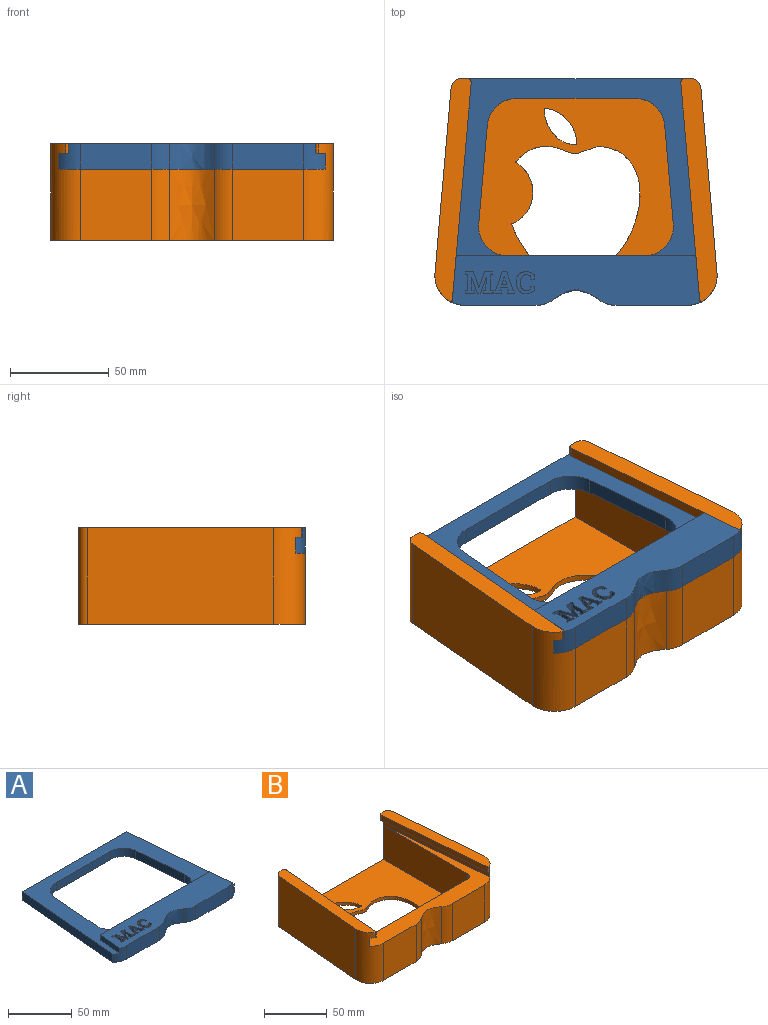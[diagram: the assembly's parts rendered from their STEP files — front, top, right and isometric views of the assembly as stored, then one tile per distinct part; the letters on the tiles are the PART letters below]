
ASSEMBLY  parts=2 mates=1
PART A: 101 faces, bbox 135.2x115x13 mm
  f0: plane 125.76x25mm, normal (0,0,1), area 2737.2mm2, adj f3,f4,f5,f6,f7,f11,f12,f15
  f1: plane 135.17x113.64mm, normal (0,0,1), area 3992.9mm2, adj f7,f8,f9,f10,f11,f13,f14,f15
  f2: plane 135.17x115mm, normal (0,0,-1), area 6927.4mm2, adj f3,f4,f5,f6,f7,f8,f9,f10
  f3: cylinder r=15mm len=13mm, axis (0,0,-1), area 125.4mm2, adj f0,f2,f4,f12
  f4: extruded ~22.62x13mm, area 325.1mm2, adj f0,f2,f3,f5
  f5: cylinder r=15mm len=13mm, axis (0,0,-1), area 125.4mm2, adj f0,f2,f4,f6
  f6: plane 36.33x13mm, normal (0,-1,0), area 472.3mm2, adj f0,f2,f5,f7
  f7: cylinder r=15mm len=13mm, axis (0,0,-1), area 130.4mm2, adj f0,f1,f2,f6,f8,f22
  f8: plane 110.25x9.59mm, normal (1,0.09,0), area 885.4mm2, adj f1,f2,f7,f9
  f9: plane 116x8mm, normal (0,1,0), area 928mm2, adj f1,f2,f8,f10
  f10: plane 110.25x9.59mm, normal (-1,0.09,0), area 885.4mm2, adj f1,f2,f9,f11
  f11: cylinder r=15mm len=13mm, axis (0,0,-1), area 130.4mm2, adj f0,f1,f2,f10,f12,f21
  f12: plane 36.33x13mm, normal (0,-1,0), area 472.3mm2, adj f0,f2,f3,f11
  f13: plane 60.16x8mm, normal (0,-1,0), area 481.3mm2, adj f1,f2,f17,f20
  f14: plane 50x8mm, normal (1,-0.09,0), area 401.5mm2, adj f1,f2,f17,f18
  f15: plane 121.65x13mm, normal (0,1,0), area 1159.1mm2, adj f0,f1,f2,f18,f19,f21,f22
  f16: plane 50x8mm, normal (-1,-0.09,0), area 401.5mm2, adj f1,f2,f19,f20
  f17: cylinder r=15mm len=14.94mm, axis (0,0,-1), area 178.1mm2, adj f1,f2,f13,f14
  f18: cylinder r=15mm len=16.3mm, axis (0,0,-1), area 198.9mm2, adj f1,f2,f14,f15
  f19: cylinder r=15mm len=16.3mm, axis (0,0,-1), area 198.9mm2, adj f1,f2,f15,f16
  f20: cylinder r=15mm len=14.94mm, axis (0,0,-1), area 178.1mm2, adj f1,f2,f13,f16
  f21: plane 23.64x5mm, normal (-1,0.09,0), area 118.6mm2, adj f0,f1,f11,f15
  f22: plane 23.64x5mm, normal (1,0.09,0), area 118.6mm2, adj f0,f1,f7,f15
  f23: plane 5x2.54mm, normal (0,-1,0), area 12.7mm2, adj f24,f42,f43,f100
  f24: plane 5x3.9mm, normal (-0.95,0.3,0), area 20.5mm2, adj f23,f25,f43,f100
  f25: plane 5x0.04mm, normal (0,1,0), area 0.2mm2, adj f24,f42,f43,f100
  f26: plane 5x0.79mm, normal (0.14,-0.99,0), area 4mm2, adj f0,f27,f41,f43
  f27: plane 5x1.33mm, normal (1,0,0), area 6.7mm2, adj f0,f26,f28,f43
  f28: plane 5x3.77mm, normal (0,1,0), area 18.9mm2, adj f0,f27,f29,f43
  f29: plane 5x1.33mm, normal (-1,0,0), area 6.7mm2, adj f0,f28,f30,f43
  f30: plane 5x0.77mm, normal (-0.18,-0.98,0), area 3.9mm2, adj f0,f29,f31,f43
  f31: plane 5x1.52mm, normal (-0.95,0.3,0), area 8mm2, adj f0,f30,f32,f43
  f32: plane 5x3.59mm, normal (0,1,0), area 18mm2, adj f0,f31,f33,f43
  f33: plane 5x1.52mm, normal (0.95,0.3,0), area 8mm2, adj f0,f32,f34,f43
  f34: plane 5x0.77mm, normal (0.17,-0.98,0), area 3.9mm2, adj f0,f33,f35,f43
  f35: plane 5x1.33mm, normal (1,0,0), area 6.7mm2, adj f0,f34,f36,f43
  f36: plane 5x3.77mm, normal (0,1,0), area 18.9mm2, adj f0,f35,f37,f43
  f37: plane 5x1.33mm, normal (-1,0,0), area 6.7mm2, adj f0,f36,f38,f43
  f38: plane 5x0.79mm, normal (-0.14,-0.99,0), area 4mm2, adj f0,f37,f39,f43
  f39: plane 9.63x5mm, normal (-0.94,-0.33,0), area 51mm2, adj f0,f38,f40,f43
  f40: plane 5x2.27mm, normal (0,-1,0), area 11.4mm2, adj f0,f39,f41,f43
  f41: plane 9.63x5mm, normal (0.94,-0.33,0), area 51mm2, adj f0,f26,f40,f43
  f42: plane 5x3.9mm, normal (0.95,0.3,0), area 20.5mm2, adj f23,f25,f43,f100
  f43: plane 11.08x10.58mm, normal (0,0,1), area 53.7mm2, adj f23,f24,f25,f26,f27,f28,f29,f30
  f44: plane 5x1.65mm, normal (0,1,0), area 8.3mm2, adj f0,f45,f67,f68
  f45: plane 5x2.19mm, normal (-1,0,0), area 11mm2, adj f0,f44,f46,f68
  f46: extruded ~5x1.71mm, area 10.6mm2, adj f0,f45,f47,f68
  f47: extruded ~5x2.32mm, area 11.9mm2, adj f0,f46,f48,f68
  f48: extruded ~5x3.66mm, area 20.5mm2, adj f0,f47,f49,f68
  f49: extruded ~5x3.97mm, area 21.6mm2, adj f0,f48,f50,f68
  f50: plane 5x0.37mm, normal (1,0,0), area 1.9mm2, adj f0,f49,f51,f68
  f51: extruded ~5x3.97mm, area 21.6mm2, adj f0,f50,f52,f68
  f52: extruded ~5x3.65mm, area 20.4mm2, adj f0,f51,f53,f68
  f53: extruded ~5x2.32mm, area 11.9mm2, adj f0,f52,f54,f68
  f54: extruded ~5x1.71mm, area 10.6mm2, adj f0,f53,f55,f68
  f55: plane 5x2.19mm, normal (-1,0,0), area 11mm2, adj f0,f54,f56,f68
  f56: plane 5x1.65mm, normal (0,-1,0), area 8.3mm2, adj f0,f55,f57,f68
  f57: plane 5x1.48mm, normal (0.99,-0.15,0), area 7.5mm2, adj f0,f56,f58,f68
  f58: extruded ~5x0.84mm, area 5mm2, adj f0,f57,f59,f68
  f59: extruded ~5x1.2mm, area 6.1mm2, adj f0,f58,f60,f68
  f60: extruded ~5x2.19mm, area 12.7mm2, adj f0,f59,f61,f68
  f61: extruded ~5x2.75mm, area 14.5mm2, adj f0,f60,f62,f68
  f62: plane 5x0.39mm, normal (-1,0,0), area 1.9mm2, adj f0,f61,f63,f68
  f63: extruded ~5x2.74mm, area 14.5mm2, adj f0,f62,f64,f68
  f64: extruded ~5x2.22mm, area 12.8mm2, adj f0,f63,f65,f68
  f65: extruded ~5x1.18mm, area 6mm2, adj f0,f64,f66,f68
  f66: extruded ~5x0.82mm, area 4.9mm2, adj f0,f65,f67,f68
  f67: plane 5x1.48mm, normal (0.99,0.15,0), area 7.5mm2, adj f0,f44,f66,f68
  f68: plane 11.4x9.11mm, normal (0,0,1), area 46.6mm2, adj f44,f45,f46,f47,f48,f49,f50,f51
  f69: plane 5x0.05mm, normal (0.16,0.99,0), area 0.2mm2, adj f0,f70,f98,f99
  f70: plane 5x4.9mm, normal (1,-0.04,0), area 24.5mm2, adj f0,f69,f71,f99
  f71: plane 5x1.74mm, normal (1,0,0), area 8.7mm2, adj f0,f70,f72,f99
  f72: plane 5x1.18mm, normal (0.19,-0.98,0), area 6mm2, adj f0,f71,f73,f99
  f73: plane 5x1.33mm, normal (1,0,0), area 6.7mm2, adj f0,f72,f74,f99
  f74: plane 5x4.59mm, normal (0,1,0), area 22.9mm2, adj f0,f73,f75,f99
  f75: plane 5x1.33mm, normal (-1,0,0), area 6.7mm2, adj f0,f74,f76,f99
  f76: plane 5x1.19mm, normal (-0.19,-0.98,0), area 6mm2, adj f0,f75,f77,f99
  f77: plane 7.95x5mm, normal (-1,0,0), area 39.8mm2, adj f0,f76,f78,f99
  f78: plane 5x1.19mm, normal (-0.19,0.98,0), area 6mm2, adj f0,f77,f79,f99
  f79: plane 5x1.34mm, normal (-1,0,0), area 6.7mm2, adj f0,f78,f80,f99
  f80: plane 5x4.09mm, normal (0,-1,0), area 20.5mm2, adj f0,f79,f81,f99
  f81: plane 8.17x5mm, normal (0.94,-0.33,0), area 43.2mm2, adj f0,f80,f82,f99
  f82: plane 5x0.05mm, normal (0,-1,0), area 0.2mm2, adj f0,f81,f83,f99
  f83: plane 8.17x5mm, normal (-0.95,-0.33,0), area 43.2mm2, adj f0,f82,f84,f99
  f84: plane 5x4.08mm, normal (0,-1,0), area 20.4mm2, adj f0,f83,f85,f99
  f85: plane 5x1.34mm, normal (1,0,0), area 6.7mm2, adj f0,f84,f86,f99
  f86: plane 5x1.18mm, normal (0.19,0.98,0), area 6mm2, adj f0,f85,f87,f99
  f87: plane 7.95x5mm, normal (1,0,0), area 39.8mm2, adj f0,f86,f88,f99
  f88: plane 5x1.18mm, normal (0.19,-0.98,0), area 6mm2, adj f0,f87,f89,f99
  f89: plane 5x1.33mm, normal (1,0,0), area 6.7mm2, adj f0,f88,f90,f99
  f90: plane 5x4.59mm, normal (0,1,0), area 22.9mm2, adj f0,f89,f91,f99
  f91: plane 5x1.33mm, normal (-1,0,0), area 6.7mm2, adj f0,f90,f92,f99
  f92: plane 5x1.19mm, normal (-0.19,-0.98,0), area 6mm2, adj f0,f91,f93,f99
  f93: plane 5x1.74mm, normal (-1,0,0), area 8.7mm2, adj f0,f92,f94,f99
  f94: plane 5x4.86mm, normal (-1,-0.04,0), area 24.3mm2, adj f0,f93,f95,f99
  f95: plane 5x0.05mm, normal (-0.16,0.99,0), area 0.2mm2, adj f0,f94,f96,f99
  f96: plane 8.17x5mm, normal (0.94,0.34,0), area 43.5mm2, adj f0,f95,f97,f99
  f97: plane 5x1.49mm, normal (0,1,0), area 7.5mm2, adj f0,f96,f98,f99
  f98: plane 8.2x5mm, normal (-0.94,0.34,0), area 43.6mm2, adj f0,f69,f97,f99
  f99: plane 13.89x11.08mm, normal (0,0,1), area 91.9mm2, adj f69,f70,f71,f72,f73,f74,f75,f76
  f100: plane 3.9x2.54mm, normal (0,0,1), area 5mm2, adj f23,f24,f25,f42
PART B: 34 faces, bbox 143.3x115x49.2 mm
  f0: plane 135.17x115mm, normal (0,0,1), area 2716mm2, adj f1,f5,f8,f9,f10,f11,f12,f21
  f1: plane 36.33x36.2mm, normal (0,-1,0), area 1315.3mm2, adj f0,f7,f21,f33
  f2: plane 116x100mm, normal (0,0,1), area 8428.4mm2, adj f3,f8,f9,f10,f19,f20,f23,f24
  f3: plane 116.83x49.2mm, normal (0,1,0), area 417.1mm2, adj f2,f7,f8,f9,f11,f12,f14,f15
  f4: plane 94.13x49.2mm, normal (-1,0.09,0), area 4648.9mm2, adj f7,f14,f21,f25
  f5: plane 36.33x36.2mm, normal (0,-1,0), area 1315.3mm2, adj f0,f7,f22,f32
  f6: plane 94.13x49.2mm, normal (1,0.09,0), area 4648.9mm2, adj f7,f18,f22,f26
  f7: plane 143.28x115mm, normal (0,0,-1), area 12235.9mm2, adj f1,f3,f4,f5,f6,f19,f20,f21
  f8: plane 94x33.2mm, normal (-1,0,0), area 3120.8mm2, adj f0,f2,f3,f24
  f9: plane 94x33.2mm, normal (1,0,0), area 3120.8mm2, adj f0,f2,f3,f23
  f10: plane 104x33.2mm, normal (0,1,0), area 3452.8mm2, adj f0,f2,f23,f24
  f11: plane 110.25x9.59mm, normal (-1,-0.09,0), area 885.4mm2, adj f0,f3,f16,f22
  f12: plane 110.25x9.59mm, normal (1,-0.09,0), area 885.4mm2, adj f0,f3,f15,f21
  f13: plane 109.97x9.56mm, normal (1,-0.09,0), area 551.9mm2, adj f14,f15,f28,f29
  f14: plane 113.06x18.46mm, normal (0,0,1), area 1088mm2, adj f3,f4,f13,f21,f25,f28,f29
  f15: plane 113.06x14.41mm, normal (0,0,-1), area 559.2mm2, adj f3,f12,f13,f21,f28,f29
  f16: plane 113.06x14.41mm, normal (0,0,-1), area 559.2mm2, adj f3,f11,f17,f22,f27,f30
  f17: plane 109.97x9.56mm, normal (-1,-0.09,0), area 551.9mm2, adj f16,f18,f27,f30
  f18: plane 113.06x18.46mm, normal (0,0,1), area 1088mm2, adj f3,f6,f17,f22,f26,f27,f30
  f19: extruded ~64.45x60.3mm, area 672.5mm2, adj f2,f7
  f20: extruded ~18.41x16.26mm, area 158.3mm2, adj f2,f7
  f21: cylinder r=15mm len=49.2mm, axis (0,0,-1), area 1085.1mm2, adj f0,f1,f4,f7,f12,f14,f15,f28
  f22: cylinder r=15mm len=49.2mm, axis (0,0,1), area 1085.1mm2, adj f0,f5,f6,f7,f11,f16,f18,f27
  f23: cylinder r=6mm len=33.2mm, axis (0,0,1), area 312.9mm2, adj f0,f2,f9,f10
  f24: cylinder r=6mm len=33.2mm, axis (0,0,-1), area 312.9mm2, adj f0,f2,f8,f10
  f25: cylinder r=5mm len=49.2mm, axis (0,0,1), area 365.1mm2, adj f3,f4,f7,f14
  f26: cylinder r=5mm len=49.2mm, axis (0,0,-1), area 365.1mm2, adj f3,f6,f7,f18
  f27: cylinder r=1mm len=5mm, axis (0,0,1), area 10.1mm2, adj f16,f17,f18,f22
  f28: cylinder r=1mm len=5mm, axis (0,0,-1), area 10.1mm2, adj f13,f14,f15,f21
  f29: cylinder r=2mm len=5mm, axis (0,0,-1), area 16.6mm2, adj f3,f13,f14,f15
  f30: cylinder r=2mm len=5mm, axis (0,0,1), area 16.6mm2, adj f3,f16,f17,f18
  f31: extruded ~36.2x22.62mm, area 905.3mm2, adj f0,f7,f32,f33
  f32: cylinder r=15mm len=36.2mm, axis (0,0,-1), area 349.2mm2, adj f0,f5,f7,f31
  f33: cylinder r=15mm len=36.2mm, axis (0,0,-1), area 349.2mm2, adj f0,f1,f7,f31
PLACE A rot(axis=(0.38,0.73,-0.56),0deg) t=(4.5,7.26,-34.53)mm
PLACE B t=(4.5,7.26,-34.53)mm
MATE slider B.f1 <-> A.f12  axis (0,-1,0) through (-33.98,-57.74,1.67)mm
